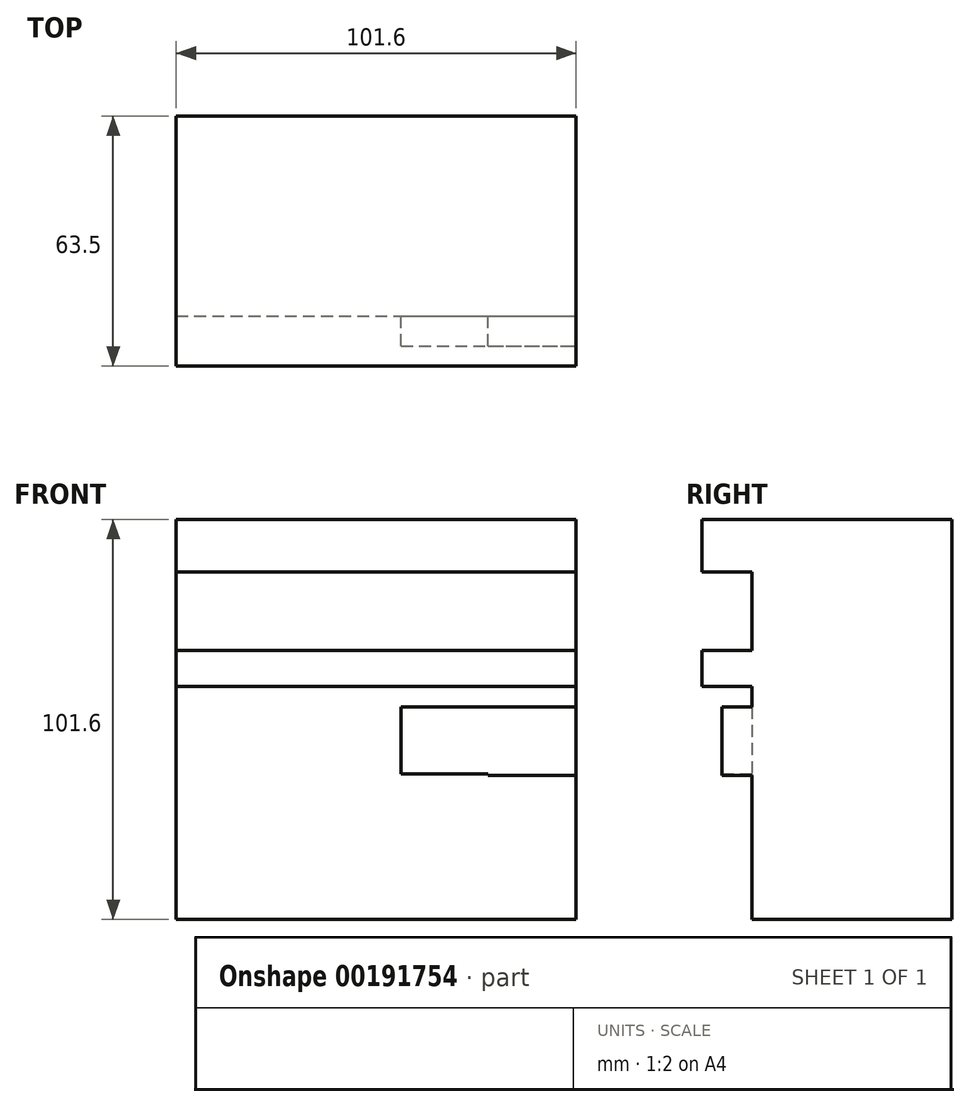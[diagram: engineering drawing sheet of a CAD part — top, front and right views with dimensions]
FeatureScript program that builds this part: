
annotation { "Feature Type Name" : "Feature", "Feature Type Description" : "" }
export const myFeature = defineFeature(function(context is Context, id is Id, definition is map)
    precondition{}
    {
        {
            var Q0;
            Q0=qCreatedBy(makeId("Front.planeOp"),FACE);
            var sketch = newSketch(context, id + "F0", { "sketchPlane" : qUnion([Q0])});
            skLineSegment(sketch, "E0.bottom", {"start": v(-75.97, 47.62) * mm, "end": v(25.63, 47.62) * mm});
            skLineSegment(sketch, "E0.top", {"start": v(-75.97, -53.98) * mm, "end": v(25.63, -53.98) * mm});
            skLineSegment(sketch, "E0.left", {"start": v(-75.97, 47.62) * mm, "end": v(-75.97, -53.98) * mm});
            skLineSegment(sketch, "E0.right", {"start": v(25.63, 47.62) * mm, "end": v(25.63, -53.98) * mm});
            skSolve(sketch);
        }
        {
            var Q0;
            Q0 = qSketchRegion(id + "F0", true);
            extrude(context, id + "F1", {"entities" : qUnion([Q0]), "depth" : 50.8 * mm});
        }
        {
            var Q0;
            Q0=makeQuery(id+"F1.opExtrude","CAP_FACE",FACE,{"disambiguationData":[OSD([sQuery(id+"F0.wireOp",EDGE,"E0.bottom"),sQuery(id+"F0.wireOp",EDGE,"E0.top"),sQuery(id+"F0.wireOp",EDGE,"E0.left"),sQuery(id+"F0.wireOp",EDGE,"E0.right")])],"isStart":false});
            var sketch = newSketch(context, id + "F2", { "sketchPlane" : qUnion([Q0])});
            skLineSegment(sketch, "E1.bottom", {"start": v(-75.97, 47.62) * mm, "end": v(25.63, 47.62) * mm});
            skLineSegment(sketch, "E1.top", {"start": v(-75.97, 34.24) * mm, "end": v(25.63, 34.24) * mm});
            skLineSegment(sketch, "E1.left", {"start": v(-75.97, 47.62) * mm, "end": v(-75.97, 34.24) * mm});
            skLineSegment(sketch, "E1.right", {"start": v(25.63, 47.62) * mm, "end": v(25.63, 34.24) * mm});
            skLineSegment(sketch, "E2.bottom", {"start": v(-75.97, 14.3) * mm, "end": v(25.63, 14.3) * mm});
            skLineSegment(sketch, "E2.top", {"start": v(-75.97, 5.15) * mm, "end": v(25.63, 5.15) * mm});
            skLineSegment(sketch, "E2.left", {"start": v(-75.97, 14.3) * mm, "end": v(-75.97, 5.15) * mm});
            skLineSegment(sketch, "E2.right", {"start": v(25.63, 14.3) * mm, "end": v(25.63, 5.15) * mm});
            skSolve(sketch);
        }
        {
            var Q0;
            Q0=makeQuery(id+"F2.imprint","IMPRINT",FACE,{"disambiguationData":[TD([[makeQuery(id+"F2.imprint","IMPRINT",EDGE,{"derivedFrom":sQuery(id+"F2.wireOp",EDGE,"E2.bottom")}),-1.0]])]});
            var Q1;
            Q1=makeQuery(id+"F2.imprint","IMPRINT",FACE,{"disambiguationData":[TD([[makeQuery(id+"F2.imprint","IMPRINT",EDGE,{"derivedFrom":sQuery(id+"F2.wireOp",EDGE,"E1.bottom")}),-1.0]])]});
            extrude(context, id + "F3", {"entities" : qUnion([Q0, Q1]), "operationType" : NewBodyOperationType.ADD, "depth" : 12.7 * mm});
        }
        {
            var Q0;
            {var subQ0=sQuery(id+"F0.wireOp",EDGE,"E0.right");var subQ1=sQuery(id+"F0.wireOp",EDGE,"E0.left");var subQ2=sQuery(id+"F0.wireOp",EDGE,"E0.top");Q0=makeQuery(id+"F3.boolean.opBoolean","SPLIT",FACE,{"disambiguationData":[TD([makeQuery(id+"F1.opExtrude","SWEPT_FACE",FACE,{"disambiguationData":[OSD([subQ2])]})])],"derivedFrom":makeQuery(id+"F1.opExtrude","CAP_FACE",FACE,{"disambiguationData":[OSD([sQuery(id+"F0.wireOp",EDGE,"E0.bottom"),subQ2,subQ1,subQ0])],"isStart":false})});}
            var sketch = newSketch(context, id + "F4", { "sketchPlane" : qUnion([Q0])});
            skLineSegment(sketch, "E3.bottom", {"start": v(-18.85, 0) * mm, "end": v(3.26, 0) * mm});
            skLineSegment(sketch, "E3.top", {"start": v(-18.85, -16.97) * mm, "end": v(3.26, -16.97) * mm});
            skLineSegment(sketch, "E3.left", {"start": v(-18.85, 0) * mm, "end": v(-18.85, -16.97) * mm});
            skLineSegment(sketch, "E3.right", {"start": v(3.26, 0) * mm, "end": v(3.26, -16.97) * mm});
            skLineSegment(sketch, "E4.bottom", {"start": v(3.26, 0) * mm, "end": v(25.63, 0) * mm});
            skLineSegment(sketch, "E4.top", {"start": v(3.26, -17.42) * mm, "end": v(25.63, -17.42) * mm});
            skLineSegment(sketch, "E4.left", {"start": v(3.26, 0) * mm, "end": v(3.26, -17.42) * mm});
            skLineSegment(sketch, "E4.right", {"start": v(25.63, 0) * mm, "end": v(25.63, -17.42) * mm});
            skSolve(sketch);
        }
        {
            var Q0;
            Q0 = qSketchRegion(id + "F4", true);
            extrude(context, id + "F5", {"entities" : qUnion([Q0]), "operationType" : NewBodyOperationType.ADD, "depth" : 7.62 * mm});
        }
    });
